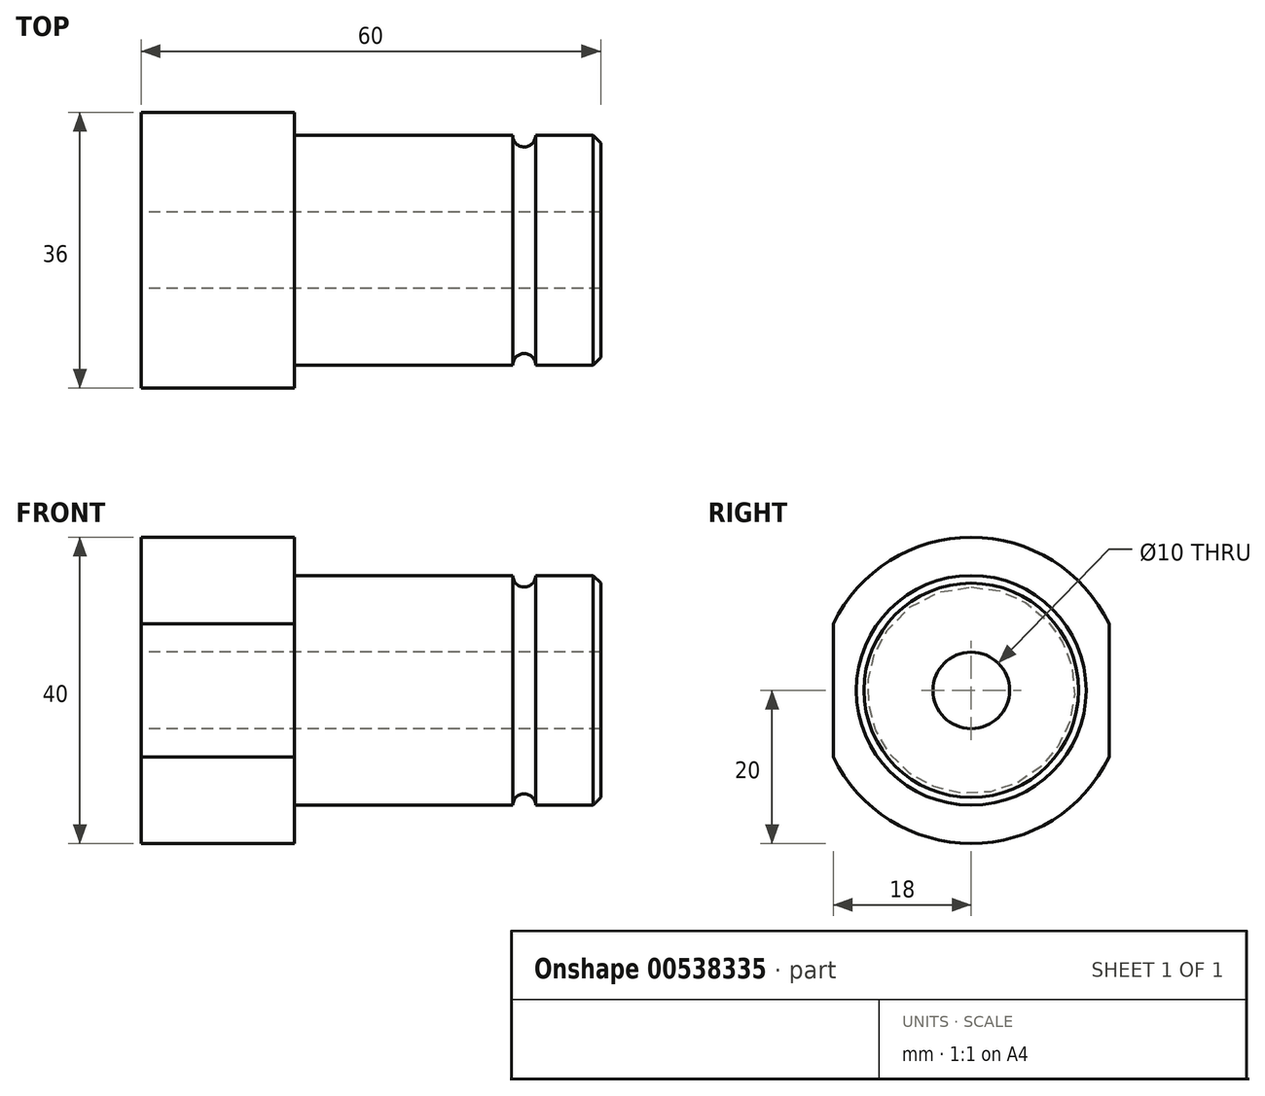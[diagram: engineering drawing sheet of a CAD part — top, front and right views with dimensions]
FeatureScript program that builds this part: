
annotation { "Feature Type Name" : "Feature", "Feature Type Description" : "" }
export const myFeature = defineFeature(function(context is Context, id is Id, definition is map)
    precondition{}
    {
        {
            var Q0;
            Q0=qCreatedBy(makeId("Front.planeOp"),FACE);
            var sketch = newSketch(context, id + "F0", { "sketchPlane" : qUnion([Q0])});
            skLineSegment(sketch, "E0", {"start": v(0, 0) * mm, "end": v(0, 20) * mm});
            skLineSegment(sketch, "E1", {"start": v(0, 20) * mm, "end": v(20, 20) * mm});
            skLineSegment(sketch, "E2", {"start": v(20, 20) * mm, "end": v(20, 15) * mm});
            skLineSegment(sketch, "E3", {"start": v(20, 15) * mm, "end": v(60, 15) * mm});
            skLineSegment(sketch, "E4", {"start": v(60, 15) * mm, "end": v(60, 0) * mm});
            skLineSegment(sketch, "E5", {"start": v(-12.34, 0) * mm, "end": v(76.6, 0) * mm, "construction": true});
            skLineSegment(sketch, "E6", {"start": v(0, 0) * mm, "end": v(60, 0) * mm});
            skSolve(sketch);
        }
        {
            var Q0;
            Q0=makeQuery(id+"F0.imprint","IMPRINT",FACE,{"disambiguationData":[TD([[makeQuery(id+"F0.imprint","IMPRINT",EDGE,{"derivedFrom":sQuery(id+"F0.wireOp",EDGE,"E0")}),-1.0]])]});
            var sketch = newSketch(context, id + "F1", { "sketchPlane" : qUnion([Q0])});
            skLineSegment(sketch, "E7", {"start": v(0, 0) * mm, "end": v(60, 0) * mm});
            skLineSegment(sketch, "E8", {"start": v(60, 0) * mm, "end": v(60, 15) * mm});
            skLineSegment(sketch, "E9", {"start": v(60, 15) * mm, "end": v(50, 15) * mm});
            skCircle(sketch, "E10", {"center": v(50, 15) * mm, "radius": 1.5 * mm});
            skSolve(sketch);
        }
        {
            var Q0;
            Q0 = qSketchRegion(id + "F0", true);
            var Q1;
            Q1=sQuery(id+"F0.wireOp",EDGE,"E6");
            revolve(context, id + "F2", {"entities" : qUnion([Q0]), "axis" : qUnion([Q1]), "revolveType" : RevolveType.FULL});
        }
        {
            var Q0;
            Q0=makeQuery(id+"F2.opRevolve","SWEPT_EDGE",EDGE,{"disambiguationData":[OSD([sQuery(id+"F0.wireOp",EDGE,"E4"),sQuery(id+"F0.wireOp",EDGE,"DP23Sca5-nVmD-abGH-QyYi-Gxn6qPcy6v3g")])]});
            chamfer(context, id + "F3", {"entities" : qUnion([Q0]), "width" : 1 * mm, "tangentPropagation" : true});
        }
        {
            var Q0;
            Q0 = qSketchRegion(id + "F1", true);
            var Q1;
            Q1=sQuery(id+"F1.wireOp",EDGE,"E7");
            revolve(context, id + "F4", {"operationType" : NewBodyOperationType.REMOVE, "entities" : qUnion([Q0]), "axis" : qUnion([Q1]), "revolveType" : RevolveType.FULL, "oppositeDirection" : true});
        }
        {
            var Q0;
            Q0=makeQuery(id+"F2.opRevolve","SWEPT_FACE",FACE,{"disambiguationData":[OSD([sQuery(id+"F0.wireOp",EDGE,"E0")])]});
            var sketch = newSketch(context, id + "F5", { "sketchPlane" : qUnion([Q0])});
            skLineSegment(sketch, "E11", {"start": v(0, -20) * mm, "end": v(-18, -20) * mm});
            skLineSegment(sketch, "E12.bottom", {"start": v(-18, -20) * mm, "end": v(18, -20) * mm});
            skLineSegment(sketch, "E12.top", {"start": v(-18, 20) * mm, "end": v(18, 20) * mm});
            skLineSegment(sketch, "E12.left", {"start": v(-18, -20) * mm, "end": v(-18, 20) * mm});
            skLineSegment(sketch, "E12.right", {"start": v(18, -20) * mm, "end": v(18, 20) * mm});
            skSolve(sketch);
        }
        {
            var Q0;
            {var subQ0=sQuery(id+"F5.wireOp",EDGE,"E12.right");var subQ1=makeQuery(id+"F2.opRevolve","SWEPT_EDGE",EDGE,{"disambiguationData":[OSD([sQuery(id+"F0.wireOp",EDGE,"E0"),sQuery(id+"F0.wireOp",EDGE,"E1")])]});var subQ2=makeQuery(id+"F5.imprint","INTERSECT",VERTEX,{"disambiguationData":[OD(0.0)],"derivedFrom":[subQ1,subQ0]});Q0=makeQuery(id+"F5.imprint","IMPRINT",FACE,{"disambiguationData":[TD([[makeQuery(id+"F5.imprint","IMPRINT",EDGE,{"disambiguationData":[TD([[subQ2,-1.0]])],"derivedFrom":subQ0}),-1.0]])]});}
            var Q1;
            {var subQ0=sQuery(id+"F5.wireOp",EDGE,"E12.left");var subQ1=makeQuery(id+"F2.opRevolve","SWEPT_EDGE",EDGE,{"disambiguationData":[OSD([sQuery(id+"F0.wireOp",EDGE,"E0"),sQuery(id+"F0.wireOp",EDGE,"E1")])]});var subQ2=makeQuery(id+"F5.imprint","INTERSECT",VERTEX,{"disambiguationData":[OD(0.0)],"derivedFrom":[subQ1,subQ0]});Q1=makeQuery(id+"F5.imprint","IMPRINT",FACE,{"disambiguationData":[TD([[makeQuery(id+"F5.imprint","IMPRINT",EDGE,{"disambiguationData":[TD([[subQ2,-1.0]])],"derivedFrom":subQ0}),1.0]])]});}
            extrude(context, id + "F6", {"entities" : qUnion([Q0, Q1]), "operationType" : NewBodyOperationType.REMOVE, "endBound" : BoundingType.UP_TO_NEXT, "oppositeDirection" : true, "depth" : 25 * mm, "offsetDistance" : 25 * mm});
        }
        {
            var Q0;
            Q0=makeQuery(id+"F2.opRevolve","SWEPT_FACE",FACE,{"disambiguationData":[OSD([sQuery(id+"F0.wireOp",EDGE,"E0")])]});
            var sketch = newSketch(context, id + "F7", { "sketchPlane" : qUnion([Q0])});
            skCircle(sketch, "E13", {"center": v(0, 0) * mm, "radius": 5 * mm});
            skSolve(sketch);
        }
        {
            var Q0;
            Q0 = qSketchRegion(id + "F7", true);
            extrude(context, id + "F8", {"entities" : qUnion([Q0]), "operationType" : NewBodyOperationType.REMOVE, "endBound" : BoundingType.UP_TO_NEXT, "oppositeDirection" : true, "depth" : 25 * mm, "offsetDistance" : 25 * mm});
        }
    });
